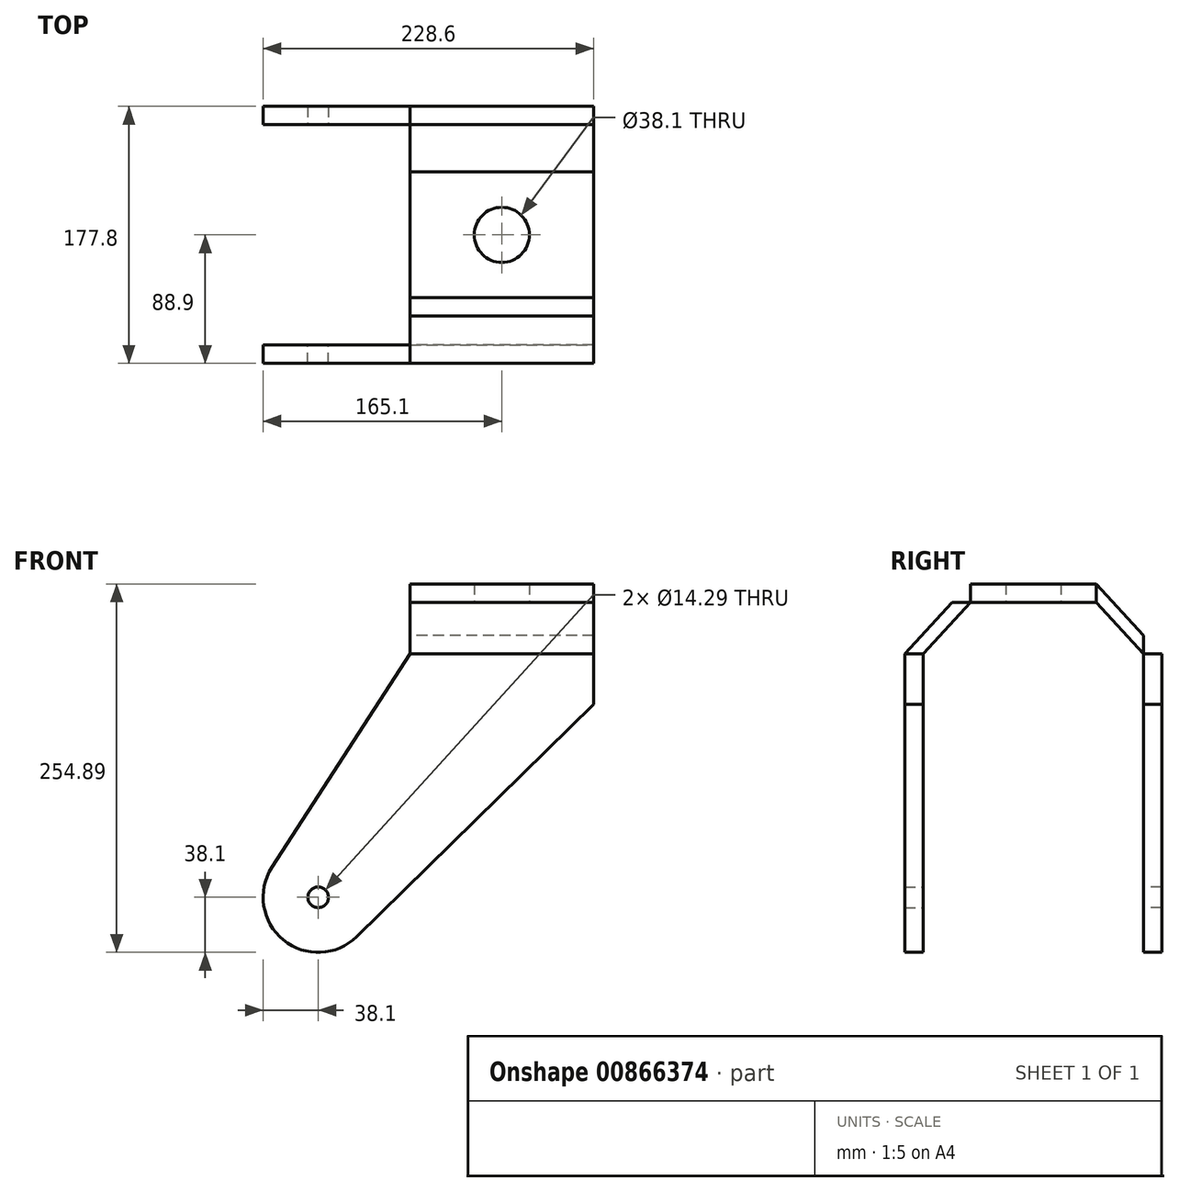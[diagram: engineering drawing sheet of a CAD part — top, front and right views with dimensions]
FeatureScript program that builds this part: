
annotation { "Feature Type Name" : "Feature", "Feature Type Description" : "" }
export const myFeature = defineFeature(function(context is Context, id is Id, definition is map)
    precondition{}
    {
        {
            var Q0;
            Q0=qCreatedBy(makeId("Front.planeOp"),FACE);
            var sketch = newSketch(context, id + "F0", { "sketchPlane" : qUnion([Q0])});
            skCircle(sketch, "E0", {"center": v(0, 0) * mm, "radius": 7.14 * mm});
            skArc(sketch, "E1", {"start": v(-31.99, 20.7) * mm, "mid": v(-24.1, -29.5) * mm, "end": v(26.67, -27.21) * mm});
            skLineSegment(sketch, "E2", {"start": v(190.5, 168.28) * mm, "end": v(190.5, 133.35) * mm});
            skLineSegment(sketch, "E3", {"start": v(63.5, 168.28) * mm, "end": v(-31.99, 20.7) * mm});
            skLineSegment(sketch, "E4", {"start": v(190.5, 133.35) * mm, "end": v(26.67, -27.21) * mm});
            skLineSegment(sketch, "E5", {"start": v(190.5, 168.28) * mm, "end": v(63.5, 168.28) * mm});
            skSolve(sketch);
        }
        {
            var Q0;
            Q0=qCreatedBy(makeId("Front.planeOp"),FACE);
            cPlane(context, id + "F1", {"entities" : qUnion([Q0]), "cplaneType" : CPlaneType.OFFSET, "offset" : 152.4 * mm, "width" : 152.4 * mm, "height" : 152.4 * mm});
        }
        {
            var Q0;
            Q0=qCreatedBy(id+"F1.planeOp",FACE);
            var sketch = newSketch(context, id + "F2", { "sketchPlane" : qUnion([Q0])});
            skCircle(sketch, "E6", {"center": v(0, 0) * mm, "radius": 7.14 * mm});
            skArc(sketch, "E7", {"start": v(-31.99, 20.7) * mm, "mid": v(-24.1, -29.5) * mm, "end": v(26.67, -27.21) * mm});
            skLineSegment(sketch, "E8", {"start": v(63.5, 168.28) * mm, "end": v(-31.99, 20.7) * mm});
            skLineSegment(sketch, "E9", {"start": v(63.5, 168.28) * mm, "end": v(190.5, 168.28) * mm});
            skLineSegment(sketch, "E10", {"start": v(190.5, 168.28) * mm, "end": v(190.5, 133.35) * mm});
            skLineSegment(sketch, "E11", {"start": v(190.5, 133.35) * mm, "end": v(26.67, -27.21) * mm});
            skSolve(sketch);
        }
        {
            var Q0;
            Q0=qCreatedBy(makeId("Top.planeOp"),FACE);
            cPlane(context, id + "F3", {"entities" : qUnion([Q0]), "cplaneType" : CPlaneType.OFFSET, "offset" : 168.27 * mm, "width" : 152.4 * mm, "height" : 152.4 * mm});
        }
        {
            var Q0;
            Q0=qCreatedBy(id+"F3.planeOp",FACE);
            cPlane(context, id + "F4", {"entities" : qUnion([Q0]), "cplaneType" : CPlaneType.OFFSET, "offset" : 35.81 * mm, "width" : 152.4 * mm, "height" : 152.4 * mm});
        }
        {
            var Q0;
            Q0=qCreatedBy(id+"F4.planeOp",FACE);
            var sketch = newSketch(context, id + "F5", { "sketchPlane" : qUnion([Q0])});
            skCircle(sketch, "E12", {"center": v(127, -76.2) * mm, "radius": 19.05 * mm});
            skLineSegment(sketch, "E13.bottom", {"start": v(190.5, -32.74) * mm, "end": v(63.5, -32.74) * mm});
            skLineSegment(sketch, "E13.top", {"start": v(190.5, -119.66) * mm, "end": v(63.5, -119.66) * mm});
            skLineSegment(sketch, "E13.left", {"start": v(190.5, -32.74) * mm, "end": v(190.5, -119.66) * mm});
            skLineSegment(sketch, "E13.right", {"start": v(63.5, -32.74) * mm, "end": v(63.5, -119.66) * mm});
            skSolve(sketch);
        }
        {
            var Q0;
            Q0=sQuery(id+"F2.wireOp",VERTEX,"E8.start");
            var Q1;
            Q1=sQuery(id+"F2.wireOp",VERTEX,"E9.end");
            var Q2;
            Q2=sQuery(id+"F5.wireOp",VERTEX,"E13.top.end");
            cPlane(context, id + "F6", {"entities" : qUnion([Q0, Q1, Q2]), "cplaneType" : CPlaneType.THREE_POINT, "offset" : 25.4 * mm, "width" : 152.4 * mm, "height" : 152.4 * mm});
        }
        {
            var Q0;
            Q0=qCreatedBy(id+"F6.planeOp",FACE);
            var sketch = newSketch(context, id + "F7", { "sketchPlane" : qUnion([Q0])});
            skLineSegment(sketch, "E14", {"start": v(-63.5, 69.9) * mm, "end": v(-63.5, 21.37) * mm});
            skLineSegment(sketch, "E15", {"start": v(-190.5, 69.9) * mm, "end": v(-190.5, 21.37) * mm});
            skLineSegment(sketch, "E16", {"start": v(-63.5, 21.37) * mm, "end": v(-190.5, 21.37) * mm});
            skLineSegment(sketch, "E17", {"start": v(-63.5, 69.9) * mm, "end": v(-190.5, 69.9) * mm});
            skSolve(sketch);
        }
        {
            var Q0;
            Q0=sQuery(id+"F0.wireOp",VERTEX,"E2.start");
            var Q1;
            Q1=sQuery(id+"F0.wireOp",VERTEX,"E3.start");
            var Q2;
            Q2=sQuery(id+"F5.wireOp",VERTEX,"E13.bottom.start");
            cPlane(context, id + "F8", {"entities" : qUnion([Q0, Q1, Q2]), "cplaneType" : CPlaneType.THREE_POINT, "offset" : 25.4 * mm, "width" : 152.4 * mm, "height" : 152.4 * mm});
        }
        {
            var Q0;
            Q0=qCreatedBy(id+"F8.planeOp",FACE);
            var sketch = newSketch(context, id + "F9", { "sketchPlane" : qUnion([Q0])});
            skLineSegment(sketch, "E18", {"start": v(190.5, 124.2) * mm, "end": v(190.5, 172.72) * mm});
            skLineSegment(sketch, "E19", {"start": v(63.5, 124.2) * mm, "end": v(63.5, 172.72) * mm});
            skLineSegment(sketch, "E20", {"start": v(190.5, 124.2) * mm, "end": v(63.5, 124.2) * mm});
            skLineSegment(sketch, "E21", {"start": v(190.5, 172.72) * mm, "end": v(63.5, 172.72) * mm});
            skSolve(sketch);
        }
        {
            var Q0;
            Q0=makeQuery(id+"F2.imprint","IMPRINT",FACE,{"disambiguationData":[TD([[makeQuery(id+"F2.imprint","IMPRINT",EDGE,{"derivedFrom":sQuery(id+"F2.wireOp",EDGE,"E6")}),-1.0]])]});
            var Q1;
            Q1=makeQuery(id+"F7.imprint","IMPRINT",FACE,{"disambiguationData":[TD([[makeQuery(id+"F7.imprint","IMPRINT",EDGE,{"derivedFrom":sQuery(id+"F7.wireOp",EDGE,"E14")}),-1.0]])]});
            extrude(context, id + "F10", {"entities" : qUnion([Q0, Q1]), "depth" : 12.7 * mm, "offsetDistance" : 25.4 * mm});
        }
        {
            var Q0;
            Q0=makeQuery(id+"F5.imprint","IMPRINT",FACE,{"disambiguationData":[TD([[makeQuery(id+"F5.imprint","IMPRINT",EDGE,{"derivedFrom":sQuery(id+"F5.wireOp",EDGE,"E12")}),-1.0]])]});
            var Q1;
            Q1=makeQuery(id+"F9.imprint","IMPRINT",FACE,{"disambiguationData":[TD([[makeQuery(id+"F9.imprint","IMPRINT",EDGE,{"derivedFrom":sQuery(id+"F9.wireOp",EDGE,"E18")}),1.0]])]});
            extrude(context, id + "F11", {"entities" : qUnion([Q0, Q1]), "depth" : 12.7 * mm, "offsetDistance" : 25.4 * mm});
        }
        {
            var Q0;
            Q0=makeQuery(id+"F0.imprint","IMPRINT",FACE,{"disambiguationData":[TD([[makeQuery(id+"F0.imprint","IMPRINT",EDGE,{"derivedFrom":sQuery(id+"F0.wireOp",EDGE,"E0")}),-1.0]])]});
            extrude(context, id + "F12", {"entities" : qUnion([Q0]), "oppositeDirection" : true, "depth" : 12.7 * mm, "offsetDistance" : 25.4 * mm});
        }
    });
